# Revit family: Track_Interior_Baso_Surface
name_source: partatom
category: Lighting Fixtures
units: mm (PartAtom-declared; Revit-internal decimal feet)

## family parameters
Cut with Voids When Loaded = No
Host = Face
Light Source = No
OmniClass Number = 23.80.70.11.17
OmniClass Title = Specialized Lighting by Location or Use
Part Type = Normal
Room Calculation Point = No
Round Connector Dimension = Use Diameter
Shared = No

## types (10) — shared parameters
Apparent Load = 0 VA
Back Side Left Turn M 90 = Joint type : Left Turn - M 90
Back Side Left Turn R 18 = Joint type : Left Turn - R 18
Back Side Left Turn R 18 XX = Joint type : Left Turn - R 18 / XX
Back Side Left Turn R 24 = Joint type : Left Turn - R 24
Back Side Left Turn R 24 XX = Joint type : Left Turn - R 24 / XX
Back Side Left Turn R 36 = Joint type : Left Turn - R 36
Back Side Left Turn R 36 XX = Joint type : Left Turn - R 36 / XX
Back Side None = Joint type : None
Back Side Right Turn M 90 = Joint type : Right Turn - M 90
Back Side Right Turn R 18 = Joint type : Right Turn - R 18
Back Side Right Turn R 18 XX = Joint type : Right Turn - R 18 / XX
Back Side Right Turn R 24 = Joint type : Right Turn - R 24
Back Side Right Turn R 24 XX = Joint type : Right Turn - R 24 / XX
Back Side Right Turn R 36 = Joint type : Right Turn - R 36
Back Side Right Turn R 36 XX = Joint type : Right Turn - R 36 / XX
Blind Covers = Blind Cover 1' flush with R1 track
CCEA = CCEA Rated(Chicago Plenum)
Default Elevation = 4' - 0"
Description = R-LINE is the next generation of low voltage track systems. Our patented technology allows you to place track heads, louver spots and curved linear insets into the curved corner of the track.
Dimmining = 0 - 10V
Field Cut = Field Cuttable Track
Front Side Left Turn M 90 = Joint type : Left Turn - M 90
Front Side Left Turn R 18 = Joint type : Left Turn - R 18
Front Side Left Turn R 18 XX = Joint type : Left Turn - R 18 / XX
Front Side Left Turn R 24 = Joint type : Left Turn - R 24
Front Side Left Turn R 24 XX = Joint type : Left Turn - R 24 / XX
Front Side Left Turn R 36 = Joint type : Left Turn - R 36
Front Side Left Turn R 36 XX = Joint type : Left Turn - R 36 / XX
Front Side None = Joint type : None
Front Side Right Turn M 90 = Joint type : Right Turn - M 90
Front Side Right Turn R 18 = Joint type : Right Turn - R 18
Front Side Right Turn R 18 XX = Joint type : Right Turn - R 18 / XX
Front Side Right Turn R 24 = Joint type : Right Turn - R 24
Front Side Right Turn R 24 XX = Joint type : Right Turn - R 24 / XX
Front Side Right Turn R 36 = Joint type : Right Turn - R 36
Front Side Right Turn R 36 XX = Joint type : Right Turn - R 36 / XX
Instruction Sheet Link = https://www.basolighting.com
Manufacturer = BASO Inc.
Model = Surface R-Line
Performance URL = https://www.basolighting.com
Power Factor = 1
Product Documentation Link = https://www.basolighting.com
Product Page URL = https://www.basolighting.com
URL = https://www.basolighting.com
Voltage = 48 V
Warranty URL = https://www.basolighting.com

## per-type parameters (varying)
| type | Custom Checker | Height | Nominal Type Length | Track Model |
| R1 Track - 2' | No | 0' - 1 1/2" | 2' - 0" | 1 |
| R1 Track - 4' | No | 0' - 1 1/2" | 4' - 0" | 1 |
| R1 Track - 6' | No | 0' - 1 1/2" | 6' - 0" | 1 |
| R1 Track - 8' | No | 0' - 1 1/2" | 8' - 0" | 1 |
| R1 Track - Custom Length | Yes | 0' - 1 1/2" | 0' - 0" | 1 |
| R2 Track - 6' | No | 0' - 2 1/2" | 6' - 0" | 2 |
| R2 Track - 8' | No | 0' - 2 1/2" | 8' - 0" | 2 |
| R2 Track - Custom Length | Yes | 0' - 2 1/2" | 0' - 0" | 2 |
| R2 Track - 4' | No | 0' - 2 1/2" | 4' - 0" | 2 |
| R2 Track - 2' | No | 0' - 2 1/2" | 2' - 0" | 2 |

## geometry (parser evidence)
native form markers: Sweep x14
no freeform markers — native parametric forms only
